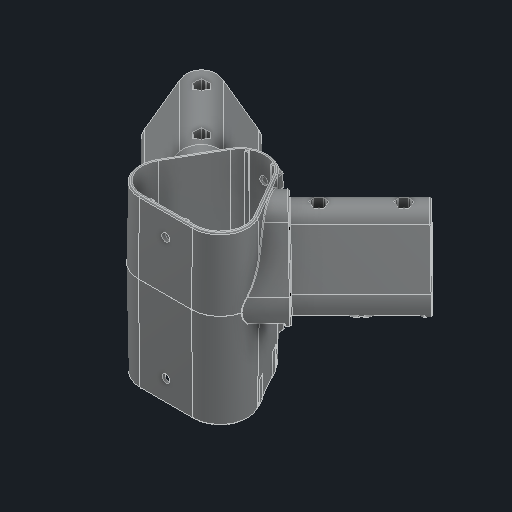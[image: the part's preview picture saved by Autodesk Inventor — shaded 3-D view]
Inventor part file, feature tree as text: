
AUTODESK INVENTOR PART (.ipt)
format: ipt  version: 2024.2 (Build 282272000, 272)  size: 2,502,144 bytes
history: native  units: in
note: dims shown in document units (in); Inventor stores cm internally (conversion verified against a paired STEP export)
features: fillet x1
ambient origin geometry x8: Origin, YZ Plane, XZ Plane, XY Plane, X Axis, Y Axis, Z Axis, Center Point
bodies: Solid1 (feature_tree)
feature tree (1):
  fillet  "Fillet139"  [1 undecoded]
note: 1 required parameter value undecoded (feature->parameter linkage not recoverable at this tier; creation-order binding heuristic only, values carry confidence <= 0.55)
